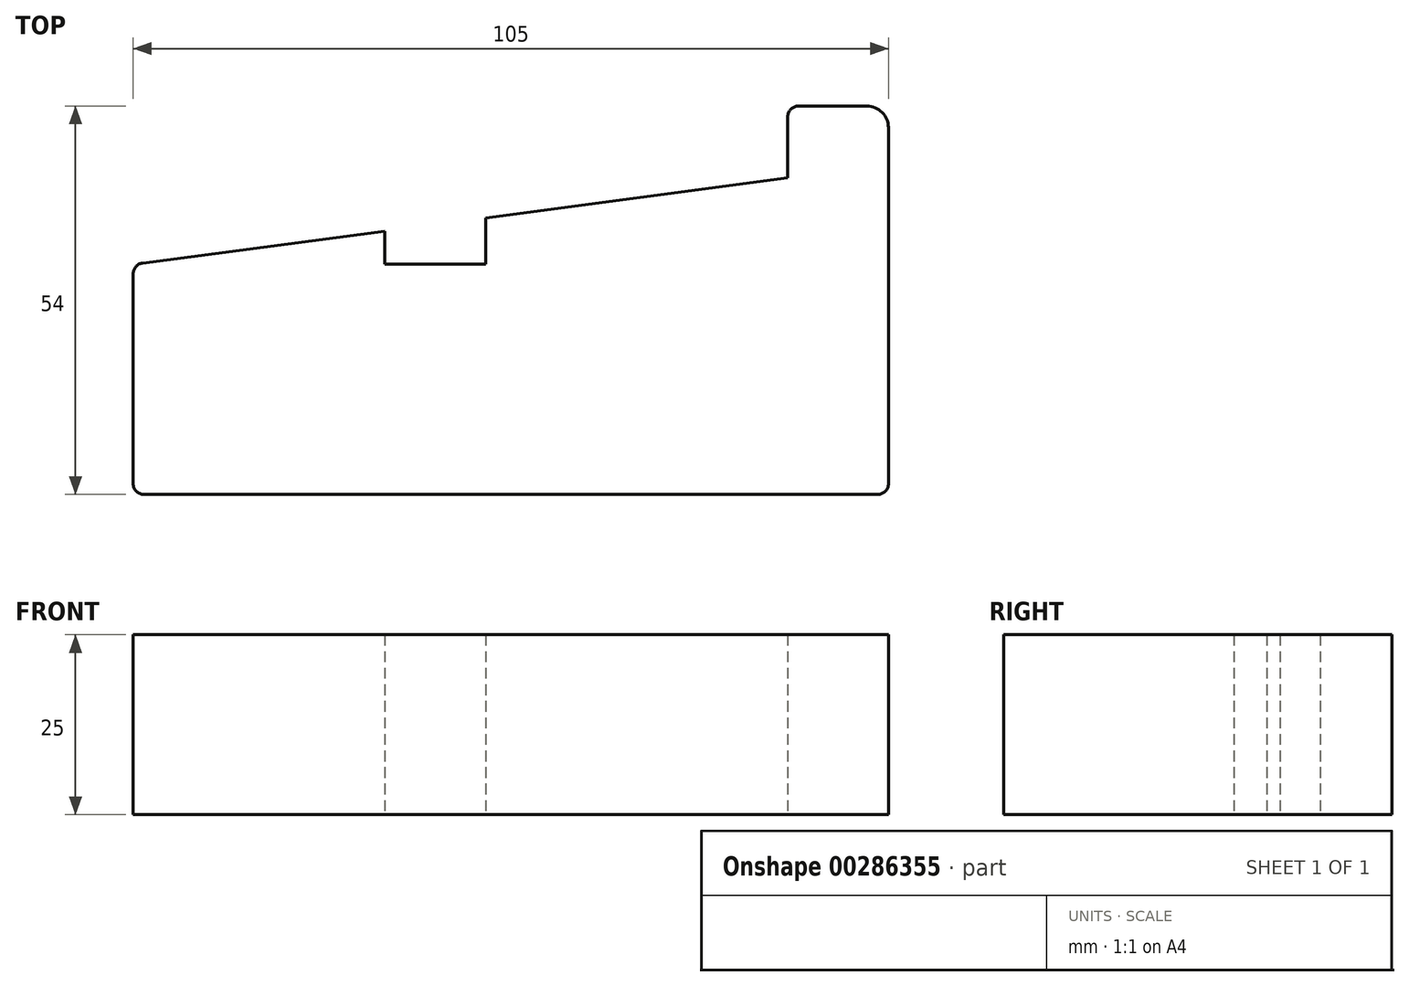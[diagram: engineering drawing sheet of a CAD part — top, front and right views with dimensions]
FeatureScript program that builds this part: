
annotation { "Feature Type Name" : "Feature", "Feature Type Description" : "" }
export const myFeature = defineFeature(function(context is Context, id is Id, definition is map)
    precondition{}
    {
        {
            var Q0;
            Q0=qCreatedBy(makeId("Top.planeOp"),FACE);
            var sketch = newSketch(context, id + "F0", { "sketchPlane" : qUnion([Q0])});
            skLineSegment(sketch, "E0", {"start": v(-63.36, -40.96) * mm, "end": v(-29.86, -40.96) * mm});
            skLineSegment(sketch, "E1", {"start": v(-29.86, -40.96) * mm, "end": v(-15.86, -40.96) * mm});
            skLineSegment(sketch, "E2", {"start": v(-15.86, -40.96) * mm, "end": v(26.14, -40.96) * mm});
            skLineSegment(sketch, "E3", {"start": v(26.14, -40.96) * mm, "end": v(38.64, -40.96) * mm});
            skLineSegment(sketch, "E4", {"start": v(40.14, -39.46) * mm, "end": v(40.14, 10.04) * mm});
            skLineSegment(sketch, "E5", {"start": v(37.14, 13.04) * mm, "end": v(27.64, 13.04) * mm});
            skLineSegment(sketch, "E6", {"start": v(26.14, 11.54) * mm, "end": v(26.14, 3.04) * mm});
            skLineSegment(sketch, "E7", {"start": v(-15.86, -8.96) * mm, "end": v(-29.86, -8.96) * mm});
            skPoint(sketch, "E8.visualSharp", {"position": v(40.14, 13.04) * mm});
            skArc(sketch, "E8.filletArc", {"start": v(40.14, 10.04) * mm, "mid": v(39.26, 12.16) * mm, "end": v(37.14, 13.04) * mm});
            skLineSegment(sketch, "E9", {"start": v(-64.86, -39.46) * mm, "end": v(-64.86, -10.28) * mm});
            skPoint(sketch, "E10.visualSharp", {"position": v(40.14, -40.96) * mm});
            skArc(sketch, "E10.filletArc", {"start": v(38.64, -40.96) * mm, "mid": v(39.7, -40.52) * mm, "end": v(40.14, -39.46) * mm});
            skPoint(sketch, "E11.visualSharp", {"position": v(26.14, 13.04) * mm});
            skArc(sketch, "E11.filletArc", {"start": v(27.64, 13.04) * mm, "mid": v(26.57, 12.6) * mm, "end": v(26.14, 11.54) * mm});
            skPoint(sketch, "E12.visualSharp", {"position": v(-64.86, -40.96) * mm});
            skArc(sketch, "E12.filletArc", {"start": v(-64.86, -39.46) * mm, "mid": v(-64.43, -40.52) * mm, "end": v(-63.36, -40.96) * mm});
            skLineSegment(sketch, "E13", {"start": v(26.14, 3.04) * mm, "end": v(-15.86, -2.5) * mm});
            skPoint(sketch, "E14.visualSharp", {"position": v(-64.86, -8.96) * mm});
            skArc(sketch, "E14.filletArc", {"start": v(-63.56, -8.79) * mm, "mid": v(-64.5, -9.29) * mm, "end": v(-64.86, -10.28) * mm});
            skLineSegment(sketch, "E15", {"start": v(-15.86, -8.96) * mm, "end": v(-15.86, -2.5) * mm});
            skLineSegment(sketch, "E16", {"start": v(-29.86, -8.96) * mm, "end": v(-29.86, -4.34) * mm});
            skLineSegment(sketch, "E17.trimOffspring", {"start": v(-29.86, -4.34) * mm, "end": v(-63.56, -8.79) * mm});
            skSolve(sketch);
        }
        {
            var Q0;
            Q0 = qSketchRegion(id + "F0", true);
            var Q1;
            Q1=makeQuery(id+"F0.imprint","IMPRINT",FACE,{"disambiguationData":[TD([[makeQuery(id+"F0.imprint","IMPRINT",EDGE,{"derivedFrom":sQuery(id+"F0.wireOp",EDGE,"E0")}),1.0]])]});
            extrude(context, id + "F1", {"entities" : qUnion([Q0, Q1]), "depth" : 25 * mm});
        }
    });
